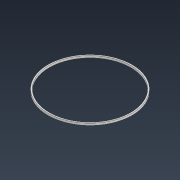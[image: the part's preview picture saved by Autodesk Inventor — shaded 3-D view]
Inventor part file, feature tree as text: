
AUTODESK INVENTOR PART (.ipt)
format: ipt  version: 2022 (Build 260153000, 153)  size: 86,016 bytes
history: native  units: mm
features: extrude x1, sketch x1
ambient origin geometry x8: Origin, YZ Plane, XZ Plane, XY Plane, X Axis, Y Axis, Z Axis, Center Point
bodies: Solid1 (feature_tree)
feature tree (2):
  extrude  "Extrusion1"  Depth=2.0mm
  sketch  "Sketch1"  dims[d0=83.0mm d1=85.5mm d2=2.0mm d3=0.0mm]
